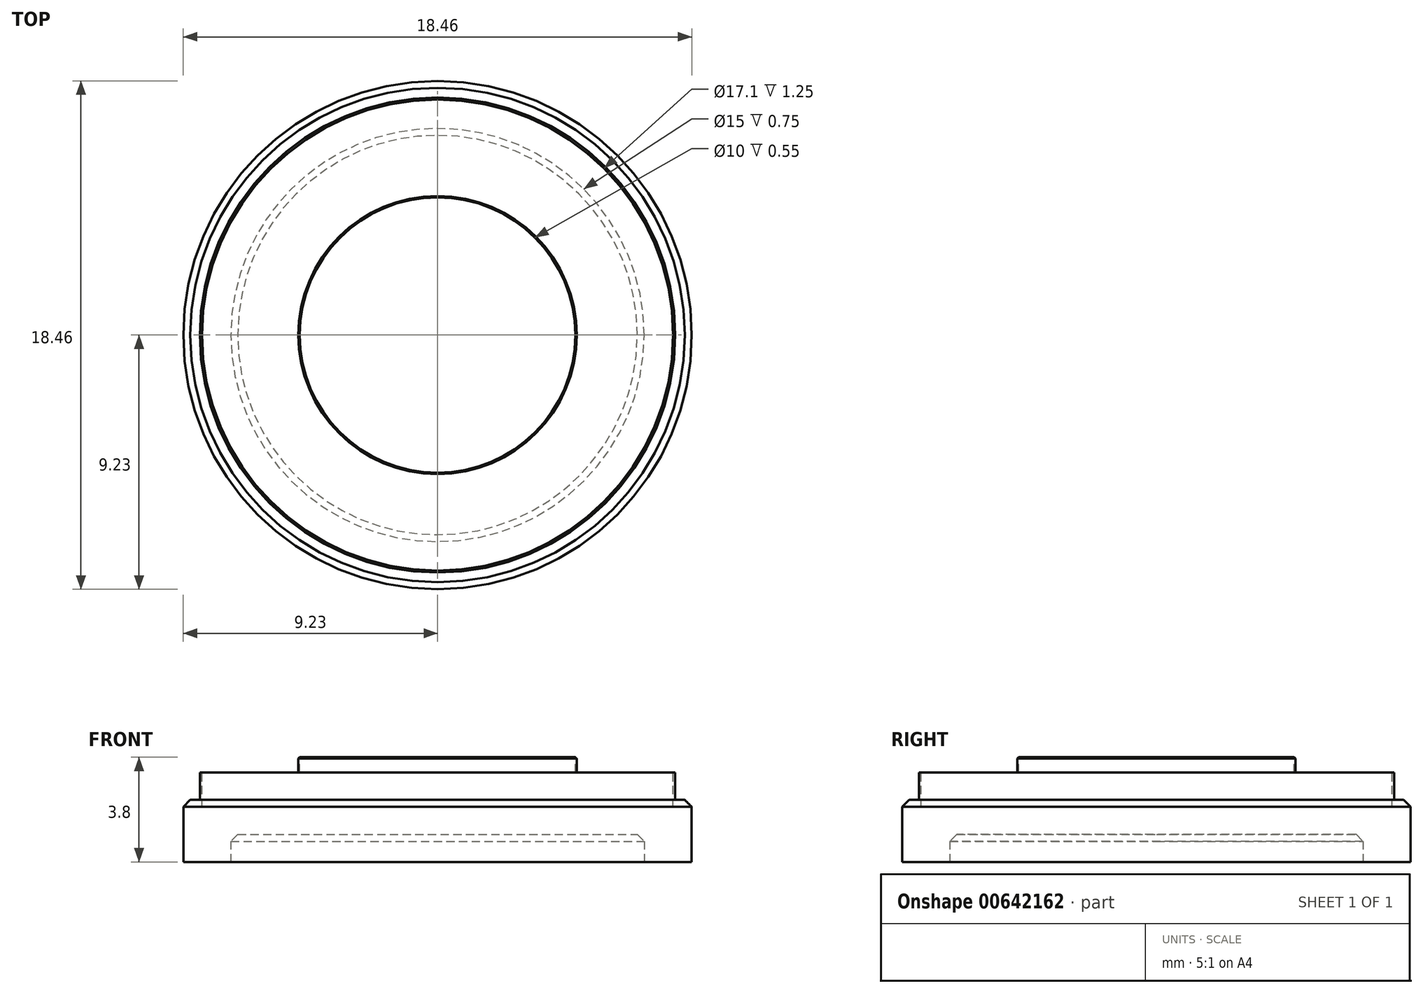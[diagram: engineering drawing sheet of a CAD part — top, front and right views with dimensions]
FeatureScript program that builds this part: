
annotation { "Feature Type Name" : "Feature", "Feature Type Description" : "" }
export const myFeature = defineFeature(function(context is Context, id is Id, definition is map)
    precondition{}
    {
        {
            var Q0;
            Q0=qCreatedBy(makeId("Top.planeOp"),FACE);
            var sketch = newSketch(context, id + "F0", { "sketchPlane" : qUnion([Q0])});
            skCircle(sketch, "E0", {"center": v(0, 0) * mm, "radius": 9.23 * mm});
            skSolve(sketch);
        }
        {
            var Q0;
            Q0 = qSketchRegion(id + "F0", true);
            extrude(context, id + "F1", {"entities" : qUnion([Q0]), "depth" : 2.25 * mm, "offsetDistance" : 25 * mm});
        }
        {
            var Q0;
            Q0=makeQuery(id+"F1.opExtrude","CAP_FACE",FACE,{"disambiguationData":[OSD([sQuery(id+"F0.wireOp",EDGE,"E0")])],"isStart":false});
            var sketch = newSketch(context, id + "F2", { "sketchPlane" : qUnion([Q0])});
            skCircle(sketch, "E1", {"center": v(0, 0) * mm, "radius": 8.62 * mm});
            skSolve(sketch);
        }
        {
            var Q0;
            Q0 = qSketchRegion(id + "F2", true);
            extrude(context, id + "F3", {"entities" : qUnion([Q0]), "operationType" : NewBodyOperationType.ADD, "depth" : 1 * mm, "offsetDistance" : 25 * mm});
        }
        {
            var Q0;
            Q0 = qSketchRegion(id + "F2", true);
            extrude(context, id + "F4", {"entities" : qUnion([Q0]), "operationType" : NewBodyOperationType.ADD, "depth" : 1 * mm, "offsetDistance" : 25 * mm});
        }
        {
            var Q0;
            Q0=makeQuery(id+"F3.opExtrude","CAP_FACE",FACE,{"disambiguationData":[OSD([sQuery(id+"F2.wireOp",EDGE,"E1")])],"isStart":false});
            var sketch = newSketch(context, id + "F5", { "sketchPlane" : qUnion([Q0])});
            skCircle(sketch, "E2", {"center": v(0, 0) * mm, "radius": 5.05 * mm});
            skSolve(sketch);
        }
        {
            var Q0;
            Q0 = qSketchRegion(id + "F5", true);
            extrude(context, id + "F6", {"entities" : qUnion([Q0]), "operationType" : NewBodyOperationType.ADD, "depth" : 0.75 * mm, "offsetDistance" : 25 * mm});
        }
        {
            var Q0;
            Q0=makeQuery(id+"F6.opExtrude","CAP_FACE",FACE,{"disambiguationData":[OSD([sQuery(id+"F5.wireOp",EDGE,"E2")])],"isStart":false});
            var sketch = newSketch(context, id + "F7", { "sketchPlane" : qUnion([Q0])});
            skCircle(sketch, "E3", {"center": v(0, 0) * mm, "radius": 5 * mm});
            skSolve(sketch);
        }
        {
            var Q0;
            Q0=makeQuery(id+"F7.imprint","IMPRINT",FACE,{"disambiguationData":[TD([[makeQuery(id+"F7.imprint","IMPRINT",EDGE,{"derivedFrom":sQuery(id+"F7.wireOp",EDGE,"E3")}),1.0]])]});
            extrude(context, id + "F8", {"entities" : qUnion([Q0]), "operationType" : NewBodyOperationType.REMOVE, "oppositeDirection" : true, "depth" : 0.75 * mm, "offsetDistance" : 25 * mm});
        }
        {
            var Q0;
            Q0=makeQuery(id+"F3.opExtrude","CAP_FACE",FACE,{"disambiguationData":[OSD([sQuery(id+"F2.wireOp",EDGE,"E1")])],"isStart":false});
            cPlane(context, id + "F9", {"entities" : qUnion([Q0]), "cplaneType" : CPlaneType.OFFSET, "offset" : 0 * mm, "width" : 150 * mm, "height" : 150 * mm});
        }
        {
            var Q0;
            Q0=qCreatedBy(id+"F9.planeOp",FACE);
            var sketch = newSketch(context, id + "F10", { "sketchPlane" : qUnion([Q0])});
            skCircle(sketch, "E4", {"center": v(0, 0) * mm, "radius": 8.55 * mm});
            skSolve(sketch);
        }
        {
            var Q0;
            Q0=makeQuery(id+"F10.imprint","IMPRINT",FACE,{"disambiguationData":[TD([[makeQuery(id+"F10.imprint","IMPRINT",EDGE,{"derivedFrom":sQuery(id+"F10.wireOp",EDGE,"E4")}),1.0]])]});
            extrude(context, id + "F11", {"entities" : qUnion([Q0]), "operationType" : NewBodyOperationType.REMOVE, "oppositeDirection" : true, "depth" : 1.25 * mm, "offsetDistance" : 25 * mm});
        }
        {
            var Q0;
            Q0=makeQuery(id+"F1.opExtrude","CAP_FACE",FACE,{"disambiguationData":[OSD([sQuery(id+"F0.wireOp",EDGE,"E0")])],"isStart":true});
            var sketch = newSketch(context, id + "F12", { "sketchPlane" : qUnion([Q0])});
            skCircle(sketch, "E5", {"center": v(0, 0) * mm, "radius": 7.5 * mm});
            skSolve(sketch);
        }
        {
            var Q0;
            Q0 = qSketchRegion(id + "F12", true);
            extrude(context, id + "F13", {"entities" : qUnion([Q0]), "operationType" : NewBodyOperationType.REMOVE, "oppositeDirection" : true, "depth" : 1 * mm, "offsetDistance" : 25 * mm});
        }
        {
            var Q0;
            Q0=makeQuery(id+"F13.boolean.opBoolean","COPY",EDGE,{"derivedFrom":makeQuery(id+"F13.opExtrude","CAP_EDGE",EDGE,{"disambiguationData":[OSD([sQuery(id+"F12.wireOp",EDGE,"E5")])],"isStart":false})});
            chamfer(context, id + "F14", {"entities" : qUnion([Q0]), "width" : 0.25 * mm, "tangentPropagation" : true});
        }
        {
            var Q0;
            Q0=makeQuery(id+"F1.opExtrude","CAP_EDGE",EDGE,{"disambiguationData":[OSD([sQuery(id+"F0.wireOp",EDGE,"E0")])],"isStart":false});
            var Q1;
            Q1=makeQuery(id+"F6.opExtrude","CAP_EDGE",EDGE,{"disambiguationData":[OSD([sQuery(id+"F5.wireOp",EDGE,"E2")])],"isStart":false});
            chamfer(context, id + "F15", {"entities" : qUnion([Q0, Q1]), "width" : 0.25 * mm, "tangentPropagation" : true});
        }
    });
